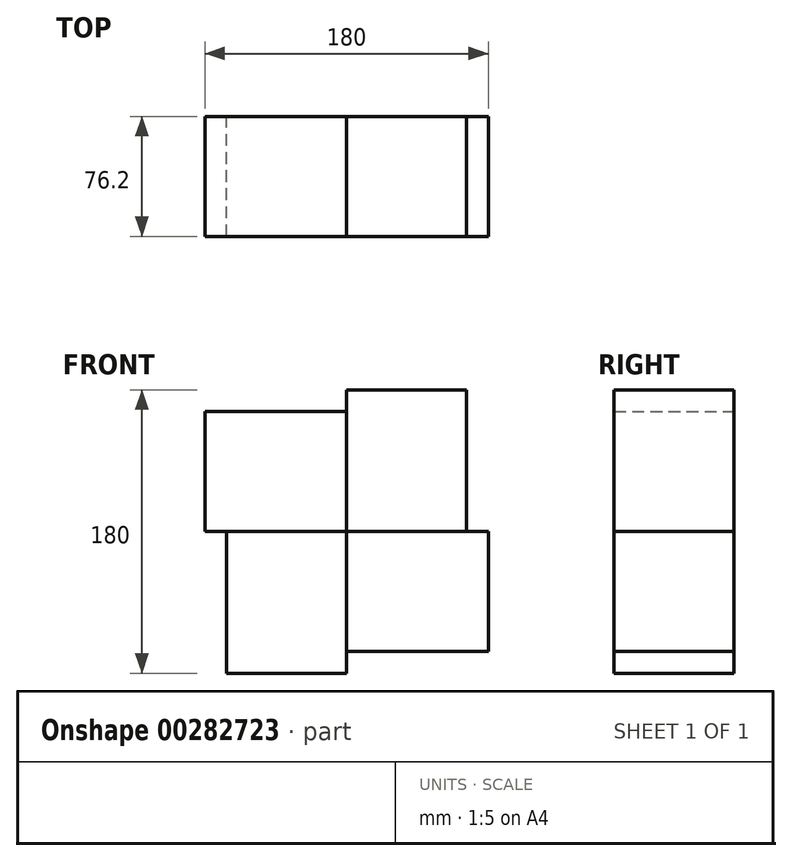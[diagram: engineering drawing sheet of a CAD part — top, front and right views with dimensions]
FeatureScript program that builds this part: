
annotation { "Feature Type Name" : "Feature", "Feature Type Description" : "" }
export const myFeature = defineFeature(function(context is Context, id is Id, definition is map)
    precondition{}
    {
        {
            var Q0;
            Q0=qCreatedBy(makeId("Top.planeOp"),FACE);
            var sketch = newSketch(context, id + "F0", { "sketchPlane" : qUnion([Q0])});
            skLineSegment(sketch, "E0.bottom", {"start": v(4.07, 0) * mm, "end": v(80.27, 0) * mm});
            skLineSegment(sketch, "E0.top", {"start": v(4.07, 76.2) * mm, "end": v(80.27, 76.2) * mm});
            skLineSegment(sketch, "E0.left", {"start": v(4.07, 0) * mm, "end": v(4.07, 76.2) * mm});
            skLineSegment(sketch, "E0.right", {"start": v(80.27, 0) * mm, "end": v(80.27, 76.2) * mm});
            skSolve(sketch);
        }
        {
            var Q0;
            Q0 = qSketchRegion(id + "F0", true);
            extrude(context, id + "F1", {"entities" : qUnion([Q0]), "depth" : 90 * mm});
        }
        {
            var Q0;
            Q0=makeQuery(id+"F1.opExtrude","SWEPT_BODY",BODY,{"disambiguationData":[OSD([sQuery(id+"F0.wireOp",EDGE,"E0.bottom"),sQuery(id+"F0.wireOp",EDGE,"E0.top"),sQuery(id+"F0.wireOp",EDGE,"E0.left"),sQuery(id+"F0.wireOp",EDGE,"E0.right")])]});
            var Q1;
            Q1=makeQuery(id+"F1.opExtrude","CAP_EDGE",EDGE,{"disambiguationData":[OSD([sQuery(id+"F0.wireOp",EDGE,"E0.right")])],"isStart":false});
            circularPattern(context, id + "F2", {"entities" : qUnion([Q0]), "axis" : qUnion([Q1]), "angle" : 360 * degree, "instanceCount" : 4, "equalSpace" : true});
        }
    });
